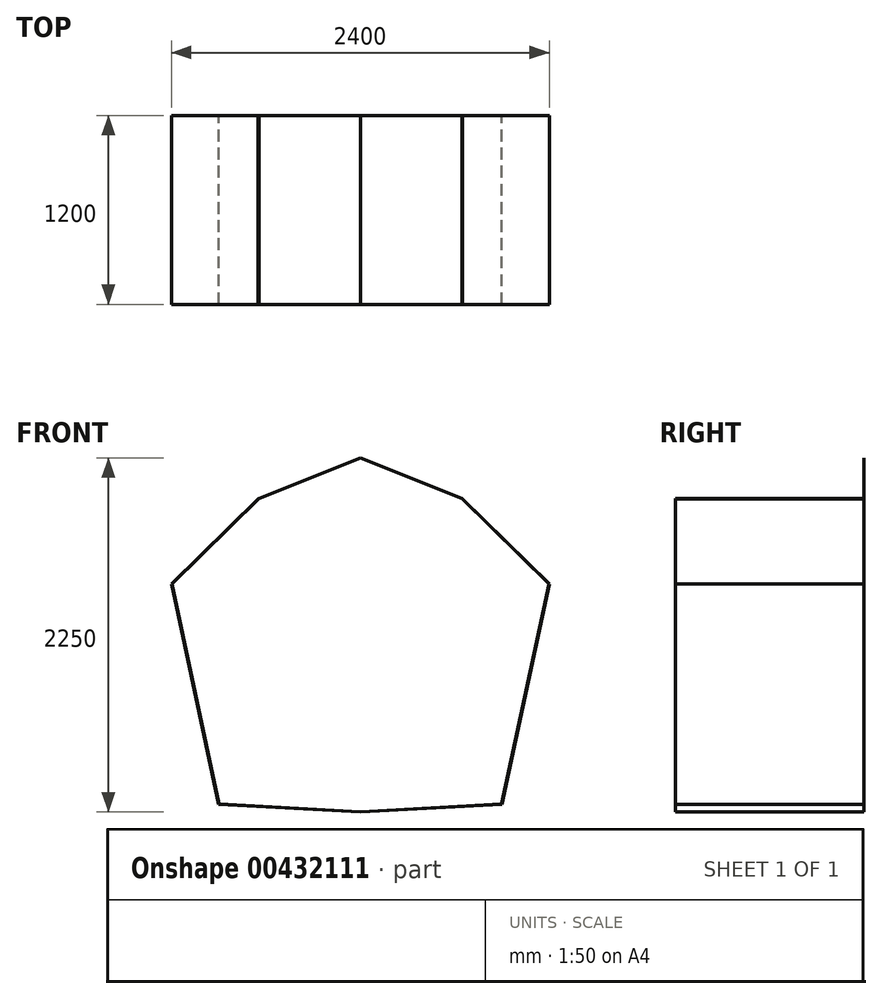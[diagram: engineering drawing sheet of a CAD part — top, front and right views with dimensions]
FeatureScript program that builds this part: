
annotation { "Feature Type Name" : "Feature", "Feature Type Description" : "" }
export const myFeature = defineFeature(function(context is Context, id is Id, definition is map)
    precondition{}
    {
        {
            var Q0;
            Q0=qCreatedBy(makeId("Front.planeOp"),FACE);
            var sketch = newSketch(context, id + "F0", { "sketchPlane" : qUnion([Q0])});
            skLineSegment(sketch, "E0", {"start": v(0, 75) * mm, "end": v(0, 1500) * mm});
            skLineSegment(sketch, "E1", {"start": v(0, 1500) * mm, "end": v(-650, 1240) * mm});
            skLineSegment(sketch, "E2", {"start": v(-650, 1240) * mm, "end": v(-1200, 700) * mm});
            skLineSegment(sketch, "E3", {"start": v(-1200, 700) * mm, "end": v(-900, -701) * mm});
            skLineSegment(sketch, "E4", {"start": v(-900, -701) * mm, "end": v(0, -750) * mm});
            skLineSegment(sketch, "E5", {"start": v(0, -750) * mm, "end": v(900, -701) * mm});
            skLineSegment(sketch, "E6", {"start": v(900, -701) * mm, "end": v(1200, 700) * mm});
            skLineSegment(sketch, "E7", {"start": v(1200, 700) * mm, "end": v(650, 1240) * mm});
            skLineSegment(sketch, "E8", {"start": v(650, 1240) * mm, "end": v(0, 1500) * mm});
            skLineSegment(sketch, "E9", {"start": v(-650, 1240) * mm, "end": v(-34.82, 66.43) * mm});
            skLineSegment(sketch, "E10", {"start": v(650, 1240) * mm, "end": v(34.82, 66.43) * mm});
            skLineSegment(sketch, "E11", {"start": v(-59.17, -46.09) * mm, "end": v(-900, -701) * mm});
            skLineSegment(sketch, "E12", {"start": v(59.17, -46.09) * mm, "end": v(900, -701) * mm});
            skLineSegment(sketch, "E13", {"start": v(1200, 700) * mm, "end": v(64.78, 37.8) * mm});
            skLineSegment(sketch, "E14", {"start": v(-64.78, 37.8) * mm, "end": v(-1200, 700) * mm});
            skLineSegment(sketch, "E15", {"start": v(0, -75) * mm, "end": v(0, -750) * mm});
            skPoint(sketch, "E16", {"position": v(-1049.9, -1) * mm});
            skPoint(sketch, "E17", {"position": v(1050.1, 0) * mm});
            skPoint(sketch, "E18", {"position": v(-997.55, -245.47) * mm});
            skPoint(sketch, "E19", {"position": v(997.76, -244.46) * mm});
            skCircle(sketch, "E20", {"center": v(0, 0) * mm, "radius": 75 * mm});
            skPoint(sketch, "E21", {"position": v(59.17, -46.09) * mm});
            skPoint(sketch, "E22", {"position": v(64.78, 37.8) * mm});
            skPoint(sketch, "E23", {"position": v(34.82, 66.43) * mm});
            skPoint(sketch, "E24", {"position": v(0, 75) * mm});
            skPoint(sketch, "E25", {"position": v(-34.82, 66.43) * mm});
            skPoint(sketch, "E26", {"position": v(-64.78, 37.8) * mm});
            skPoint(sketch, "E27", {"position": v(-59.17, -46.09) * mm});
            skPoint(sketch, "E28", {"position": v(0, -75) * mm});
            skSolve(sketch);
        }
        {
            var Q0;
            Q0=makeQuery(id+"F0.imprint","IMPRINT",FACE,{"disambiguationData":[TD([[makeQuery(id+"F0.imprint","IMPRINT",EDGE,{"derivedFrom":sQuery(id+"F0.wireOp",EDGE,"E6")}),1.0]])]});
            var Q1;
            Q1=makeQuery(id+"F0.imprint","IMPRINT",FACE,{"disambiguationData":[TD([[makeQuery(id+"F0.imprint","IMPRINT",EDGE,{"derivedFrom":sQuery(id+"F0.wireOp",EDGE,"E5")}),1.0]])]});
            var Q2;
            Q2=makeQuery(id+"F0.imprint","IMPRINT",FACE,{"disambiguationData":[TD([[makeQuery(id+"F0.imprint","IMPRINT",EDGE,{"derivedFrom":sQuery(id+"F0.wireOp",EDGE,"E4")}),1.0]])]});
            var Q3;
            Q3=makeQuery(id+"F0.imprint","IMPRINT",FACE,{"disambiguationData":[TD([[makeQuery(id+"F0.imprint","IMPRINT",EDGE,{"derivedFrom":sQuery(id+"F0.wireOp",EDGE,"E3")}),1.0]])]});
            var Q4;
            Q4=makeQuery(id+"F0.imprint","IMPRINT",FACE,{"disambiguationData":[TD([[makeQuery(id+"F0.imprint","IMPRINT",EDGE,{"derivedFrom":sQuery(id+"F0.wireOp",EDGE,"E2")}),1.0]])]});
            var Q5;
            {var subQ0=sQuery(id+"F0.wireOp",EDGE,"E0");Q5=makeQuery(id+"F0.imprint","IMPRINT",FACE,{"disambiguationData":[TD([[makeQuery(id+"F0.imprint","IMPRINT",EDGE,{"derivedFrom":subQ0}),1.0]])]});}
            var Q6;
            {var subQ0=sQuery(id+"F0.wireOp",EDGE,"E0");Q6=makeQuery(id+"F0.imprint","IMPRINT",FACE,{"disambiguationData":[TD([[makeQuery(id+"F0.imprint","IMPRINT",EDGE,{"derivedFrom":subQ0}),-1.0]])]});}
            var Q7;
            Q7=makeQuery(id+"F0.imprint","IMPRINT",FACE,{"disambiguationData":[TD([[makeQuery(id+"F0.imprint","IMPRINT",EDGE,{"derivedFrom":sQuery(id+"F0.wireOp",EDGE,"E7")}),1.0]])]});
            var Q8;
            {var subQ0=sQuery(id+"F0.wireOp",EDGE,"E20");var subQ4=makeQuery(id+"F0.imprint","INTERSECT",VERTEX,{"derivedFrom":[sQuery(id+"F0.wireOp",EDGE,"E10"),subQ0]});Q8=makeQuery(id+"F0.imprint","IMPRINT",FACE,{"disambiguationData":[TD([[makeQuery(id+"F0.imprint","IMPRINT",EDGE,{"disambiguationData":[TD([[subQ4,1.0]])],"derivedFrom":subQ0}),1.0]])]});}
            extrude(context, id + "F1", {"entities" : qUnion([Q0, Q1, Q2, Q3, Q4, Q5, Q6, Q7, Q8]), "depth" : 1200 * mm, "offsetDistance" : 25 * mm});
        }
        {
            var Q0;
            Q0=makeQuery(id+"F1.opExtrude","SWEPT_FACE",FACE,{"disambiguationData":[OSD([sQuery(id+"F0.wireOp",EDGE,"E1")])]});
            var Q1;
            Q1=makeQuery(id+"F1.opExtrude","SWEPT_FACE",FACE,{"disambiguationData":[OSD([sQuery(id+"F0.wireOp",EDGE,"E8")])]});
            var Q2;
            Q2=makeQuery(id+"F1.opExtrude","CAP_FACE",FACE,{"disambiguationData":[OSD([sQuery(id+"F0.wireOp",EDGE,"E1"),sQuery(id+"F0.wireOp",EDGE,"E2"),sQuery(id+"F0.wireOp",EDGE,"E3"),sQuery(id+"F0.wireOp",EDGE,"E4"),sQuery(id+"F0.wireOp",EDGE,"E5"),sQuery(id+"F0.wireOp",EDGE,"E6"),sQuery(id+"F0.wireOp",EDGE,"E7"),sQuery(id+"F0.wireOp",EDGE,"E8"),sQuery(id+"F0.wireOp",EDGE,"E20")])],"isStart":false});
            shell(context, id + "F2", {"entities" : qUnion([Q0, Q1, Q2]), "thickness" : 2.5 * mm});
        }
        {
            var Q0;
            Q0=sQuery(id+"F0.wireOp",EDGE,"E20");
            extrude(context, id + "F3", {"bodyType" : ToolBodyType.SURFACE, "surfaceEntities" : qUnion([Q0]), "depth" : 10 * mm, "offsetDistance" : 25 * mm});
        }
    });
